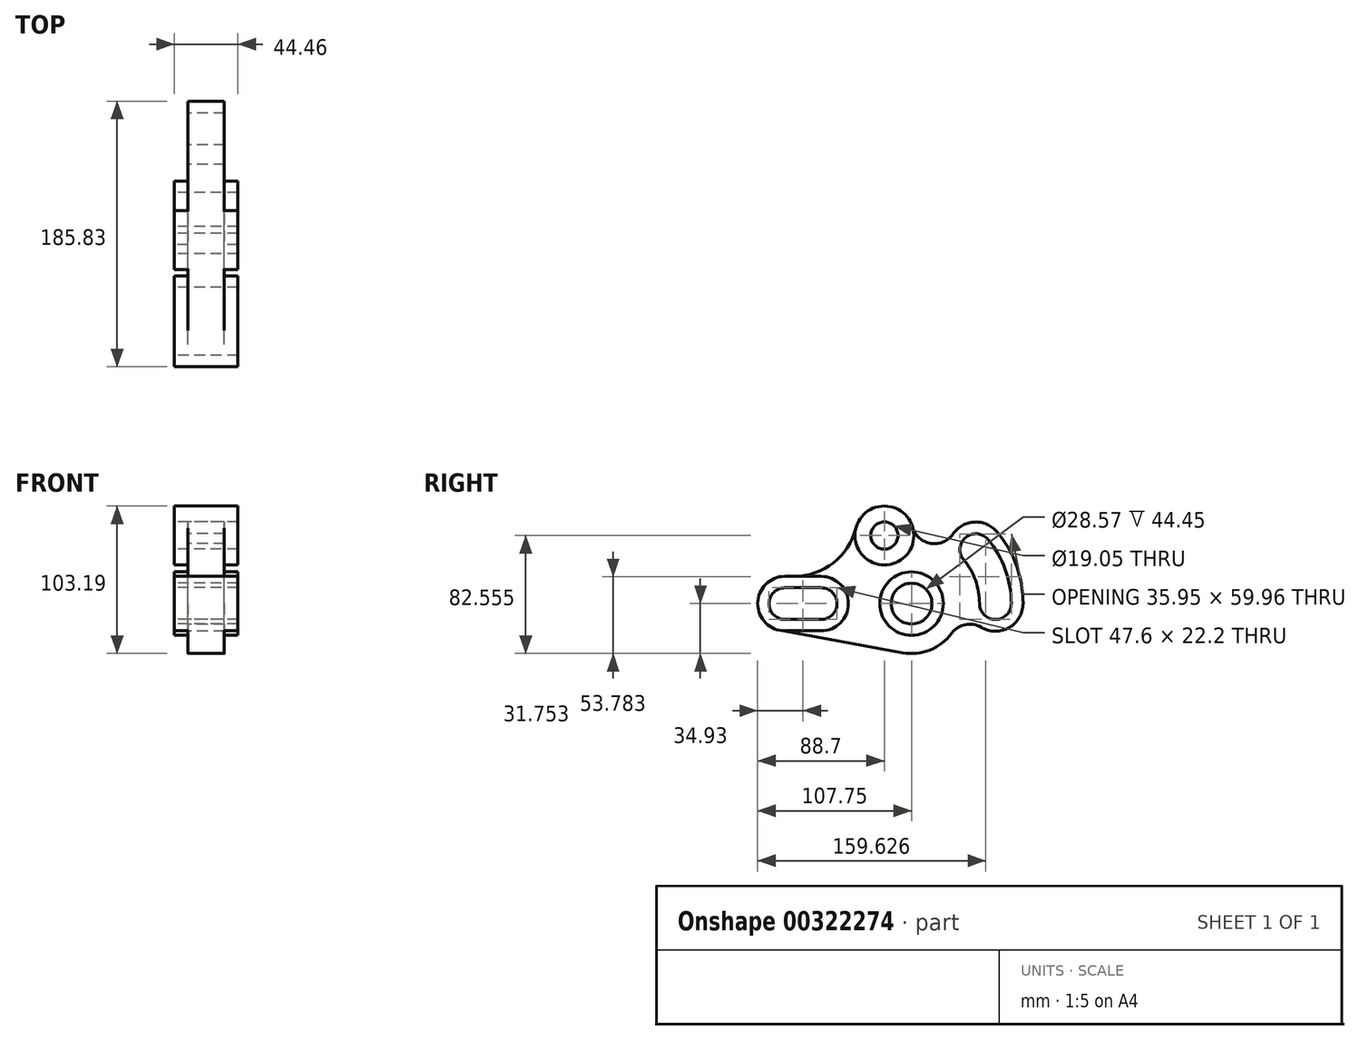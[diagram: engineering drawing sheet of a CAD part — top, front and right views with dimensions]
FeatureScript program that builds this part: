
annotation { "Feature Type Name" : "Feature", "Feature Type Description" : "" }
export const myFeature = defineFeature(function(context is Context, id is Id, definition is map)
    precondition{}
    {
        {
            var Q0;
            Q0=qCreatedBy(makeId("Right.planeOp"),FACE);
            var sketch = newSketch(context, id + "F0", { "sketchPlane" : qUnion([Q0])});
            skCircle(sketch, "E0", {"center": v(0, 0) * mm, "radius": 14.29 * mm});
            skCircle(sketch, "E1", {"center": v(0, 0) * mm, "radius": 22.23 * mm});
            skCircle(sketch, "E2", {"center": v(-19.05, 47.63) * mm, "radius": 9.53 * mm});
            skCircle(sketch, "E3", {"center": v(-19.05, 47.63) * mm, "radius": 20.64 * mm});
            skLineSegment(sketch, "E4", {"start": v(0, 86.11) * mm, "end": v(0, -85.54) * mm, "construction": true});
            skLineSegment(sketch, "E5", {"start": v(-22.22, 0) * mm, "end": v(148.48, 0) * mm, "construction": true});
            skLineSegment(sketch, "E6", {"start": v(-19.05, 26.99) * mm, "end": v(-19.05, 86.6) * mm, "construction": true});
            skLineSegment(sketch, "E7", {"start": v(0, 0) * mm, "end": v(108.33, 90.9) * mm, "construction": true});
            skLineSegment(sketch, "E8", {"start": v(-22.22, 0) * mm, "end": v(-138.7, 0) * mm, "construction": true});
            skArc(sketch, "E9", {"start": v(47.6, 0) * mm, "mid": v(58.72, -11.13) * mm, "end": v(69.85, 0) * mm});
            skArc(sketch, "E10", {"start": v(53.5, 44.9) * mm, "mid": v(37.83, 46.27) * mm, "end": v(36.46, 30.6) * mm});
            skArc(sketch, "E11", {"start": v(47.6, 0) * mm, "mid": v(44.73, 16.28) * mm, "end": v(36.46, 30.6) * mm});
            skArc(sketch, "E12", {"start": v(69.85, 0) * mm, "mid": v(65.64, 23.9) * mm, "end": v(53.5, 44.9) * mm});
            skArc(sketch, "E13", {"start": v(-88.7, 11.1) * mm, "mid": v(-99.8, 0) * mm, "end": v(-88.7, -11.1) * mm});
            skArc(sketch, "E14", {"start": v(-63.3, -11.1) * mm, "mid": v(-52.2, 0) * mm, "end": v(-63.3, 11.1) * mm});
            skLineSegment(sketch, "E15", {"start": v(-88.7, -11.1) * mm, "end": v(-63.3, -11.1) * mm});
            skLineSegment(sketch, "E16", {"start": v(-88.7, 11.1) * mm, "end": v(-63.3, 11.1) * mm});
            skArc(sketch, "E17", {"start": v(-88.7, 19.05) * mm, "mid": v(-107.75, 0) * mm, "end": v(-88.7, -19.05) * mm});
            skArc(sketch, "E18", {"start": v(-63.3, -19.05) * mm, "mid": v(-44.25, 0) * mm, "end": v(-63.3, 19.05) * mm});
            skLineSegment(sketch, "E19", {"start": v(-88.7, 19.05) * mm, "end": v(-63.3, 19.05) * mm});
            skLineSegment(sketch, "E20", {"start": v(-88.7, -19.05) * mm, "end": v(-63.3, -19.05) * mm});
            skArc(sketch, "E21", {"start": v(-82.17, 19.05) * mm, "mid": v(-54.84, 28.45) * mm, "end": v(-39.06, 52.66) * mm});
            skLineSegment(sketch, "E22", {"start": v(-92.1, -18.74) * mm, "end": v(-6.25, -34.36) * mm});
            skArc(sketch, "E23", {"start": v(-6.25, -34.36) * mm, "mid": v(12.82, -32.49) * mm, "end": v(28.03, -20.84) * mm});
            skArc(sketch, "E24", {"start": v(48.86, -16.65) * mm, "mid": v(37.64, -14.74) * mm, "end": v(28.03, -20.84) * mm});
            skArc(sketch, "E25", {"start": v(78.08, 0) * mm, "mid": v(73.37, 26.7) * mm, "end": v(59.81, 50.19) * mm});
            skArc(sketch, "E26", {"start": v(59.81, 50.19) * mm, "mid": v(44.09, 57.08) * mm, "end": v(29.07, 48.76) * mm});
            skArc(sketch, "E27", {"start": v(48.86, -16.65) * mm, "mid": v(68.3, -16.81) * mm, "end": v(78.08, 0) * mm});
            skArc(sketch, "E28", {"start": v(0.77, 53.37) * mm, "mid": v(13.46, 42.13) * mm, "end": v(29.07, 48.76) * mm});
            skSolve(sketch);
        }
        {
            var Q0;
            Q0=makeQuery(id+"F0.imprint","IMPRINT",FACE,{"disambiguationData":[TD([[makeQuery(id+"F0.imprint","IMPRINT",EDGE,{"derivedFrom":sQuery(id+"F0.wireOp",EDGE,"E1")}),-1.0]])]});
            extrude(context, id + "F1", {"entities" : qUnion([Q0]), "depth" : 25.4 * mm, "symmetric" : true});
        }
        {
            var Q0;
            Q0=makeQuery(id+"F0.imprint","IMPRINT",FACE,{"disambiguationData":[TD([[makeQuery(id+"F0.imprint","IMPRINT",EDGE,{"derivedFrom":sQuery(id+"F0.wireOp",EDGE,"E13")}),-1.0]])]});
            var Q1;
            Q1=makeQuery(id+"F0.imprint","IMPRINT",FACE,{"disambiguationData":[TD([[makeQuery(id+"F0.imprint","IMPRINT",EDGE,{"derivedFrom":sQuery(id+"F0.wireOp",EDGE,"E2")}),-1.0]])]});
            var Q2;
            Q2=makeQuery(id+"F0.imprint","IMPRINT",FACE,{"disambiguationData":[TD([[makeQuery(id+"F0.imprint","IMPRINT",EDGE,{"derivedFrom":sQuery(id+"F0.wireOp",EDGE,"E0")}),-1.0]])]});
            extrude(context, id + "F2", {"entities" : qUnion([Q0, Q1, Q2]), "operationType" : NewBodyOperationType.ADD, "depth" : 44.45 * mm, "symmetric" : true});
        }
    });
